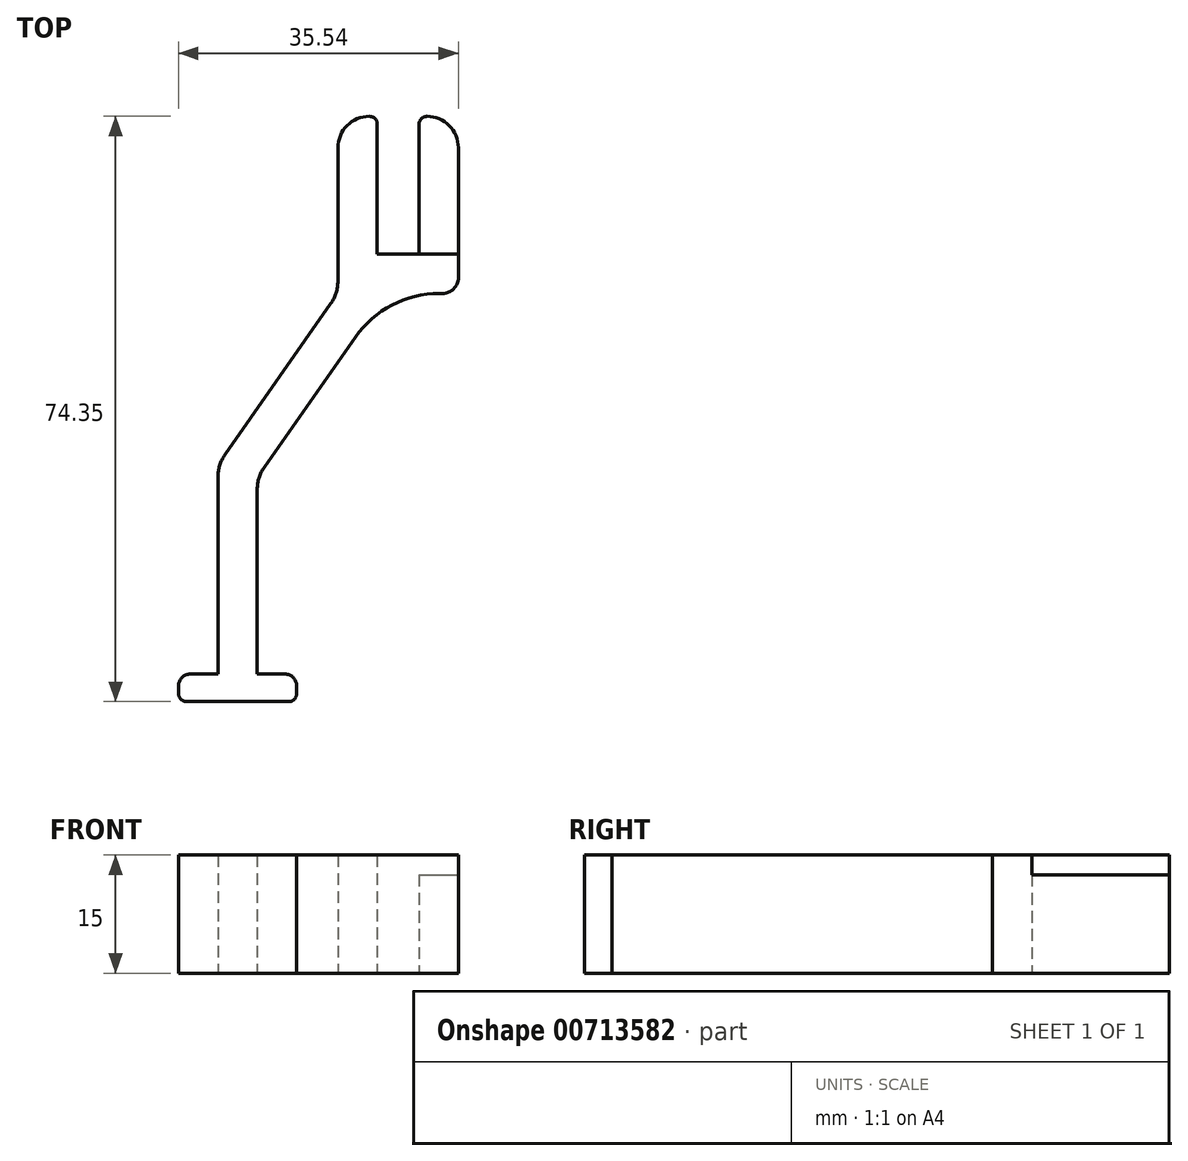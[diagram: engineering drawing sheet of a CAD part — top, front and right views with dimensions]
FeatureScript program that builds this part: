
annotation { "Feature Type Name" : "Feature", "Feature Type Description" : "" }
export const myFeature = defineFeature(function(context is Context, id is Id, definition is map)
    precondition{}
    {
        {
            var Q0;
            Q0=qCreatedBy(makeId("Top.planeOp"),FACE);
            var sketch = newSketch(context, id + "F0", { "sketchPlane" : qUnion([Q0])});
            skLineSegment(sketch, "E0", {"start": v(0, 0) * mm, "end": v(0, 16.5) * mm});
            skLineSegment(sketch, "E1", {"start": v(0, 0) * mm, "end": v(-5.3, 0) * mm});
            skLineSegment(sketch, "E2", {"start": v(-5.3, 0) * mm, "end": v(-5.3, 16.5) * mm});
            skLineSegment(sketch, "E3", {"start": v(1, 17.5) * mm, "end": v(1, 17.5) * mm});
            skLineSegment(sketch, "E4", {"start": v(5, 13.5) * mm, "end": v(5, -3.42) * mm});
            skLineSegment(sketch, "E5", {"start": v(-6.3, 17.5) * mm, "end": v(-6.3, 17.5) * mm});
            skLineSegment(sketch, "E6", {"start": v(-10.3, 13.5) * mm, "end": v(-10.3, -3) * mm});
            skLineSegment(sketch, "E7", {"start": v(5.9, -6.3) * mm, "end": v(19.34, -25.48) * mm});
            skLineSegment(sketch, "E8.0", {"start": v(2.78, -10.54) * mm, "end": v(14.34, -27.06) * mm});
            skLineSegment(sketch, "E9", {"start": v(-8.3, -5) * mm, "end": v(-7.87, -5) * mm});
            skPoint(sketch, "E10.visualSharp", {"position": v(-1.1, -5) * mm});
            skArc(sketch, "E10.filletArc", {"start": v(2.78, -10.54) * mm, "mid": v(-1.87, -6.47) * mm, "end": v(-7.87, -5) * mm});
            skPoint(sketch, "E11.visualSharp", {"position": v(-10.3, 17.5) * mm});
            skArc(sketch, "E11.filletArc", {"start": v(-6.3, 17.5) * mm, "mid": v(-9.13, 16.33) * mm, "end": v(-10.3, 13.5) * mm});
            skPoint(sketch, "E12.visualSharp", {"position": v(-5.3, 17.5) * mm});
            skArc(sketch, "E12.filletArc", {"start": v(-5.3, 16.5) * mm, "mid": v(-5.6, 17.2) * mm, "end": v(-6.3, 17.5) * mm});
            skPoint(sketch, "E13.visualSharp", {"position": v(5, 17.5) * mm});
            skArc(sketch, "E13.filletArc", {"start": v(5, 13.5) * mm, "mid": v(3.83, 16.33) * mm, "end": v(1, 17.5) * mm});
            skPoint(sketch, "E14.visualSharp", {"position": v(0, 17.5) * mm});
            skArc(sketch, "E14.filletArc", {"start": v(1, 17.5) * mm, "mid": v(0.3, 17.2) * mm, "end": v(0, 16.5) * mm});
            skPoint(sketch, "E15.visualSharp", {"position": v(5, -5) * mm});
            skArc(sketch, "E15.filletArc", {"start": v(5, -3.42) * mm, "mid": v(5.23, -4.93) * mm, "end": v(5.9, -6.3) * mm});
            skPoint(sketch, "E16.visualSharp", {"position": v(-10.3, -5) * mm});
            skArc(sketch, "E16.filletArc", {"start": v(-10.3, -3) * mm, "mid": v(-9.71, -4.41) * mm, "end": v(-8.3, -5) * mm});
            skLineSegment(sketch, "E17", {"start": v(15.24, -29.92) * mm, "end": v(15.24, -53.35) * mm});
            skLineSegment(sketch, "E18.0", {"start": v(20.24, -28.35) * mm, "end": v(20.24, -53.35) * mm});
            skPoint(sketch, "E19.visualSharp", {"position": v(20.24, -26.77) * mm});
            skArc(sketch, "E19.filletArc", {"start": v(20.24, -28.35) * mm, "mid": v(20.01, -26.84) * mm, "end": v(19.34, -25.48) * mm});
            skArc(sketch, "E20.filletArc", {"start": v(15.24, -29.92) * mm, "mid": v(15.01, -28.42) * mm, "end": v(14.34, -27.06) * mm});
            skLineSegment(sketch, "E21", {"start": v(20.24, -53.35) * mm, "end": v(23.74, -53.35) * mm});
            skLineSegment(sketch, "E22", {"start": v(15.24, -53.35) * mm, "end": v(11.74, -53.35) * mm});
            skLineSegment(sketch, "E23", {"start": v(10.24, -54.85) * mm, "end": v(10.24, -55.85) * mm});
            skLineSegment(sketch, "E24", {"start": v(25.24, -54.85) * mm, "end": v(25.24, -55.85) * mm});
            skLineSegment(sketch, "E25", {"start": v(24.24, -56.85) * mm, "end": v(11.24, -56.85) * mm});
            skPoint(sketch, "E26.visualSharp", {"position": v(10.24, -53.35) * mm});
            skArc(sketch, "E26.filletArc", {"start": v(11.74, -53.35) * mm, "mid": v(10.68, -53.79) * mm, "end": v(10.24, -54.85) * mm});
            skPoint(sketch, "E27.visualSharp", {"position": v(25.24, -53.35) * mm});
            skArc(sketch, "E27.filletArc", {"start": v(25.24, -54.85) * mm, "mid": v(24.8, -53.79) * mm, "end": v(23.74, -53.35) * mm});
            skPoint(sketch, "E28.visualSharp", {"position": v(25.24, -56.85) * mm});
            skArc(sketch, "E28.filletArc", {"start": v(24.24, -56.85) * mm, "mid": v(24.95, -56.55) * mm, "end": v(25.24, -55.85) * mm});
            skPoint(sketch, "E29.visualSharp", {"position": v(10.24, -56.85) * mm});
            skArc(sketch, "E29.filletArc", {"start": v(10.24, -55.85) * mm, "mid": v(10.54, -56.55) * mm, "end": v(11.24, -56.85) * mm});
            skSolve(sketch);
        }
        {
            var Q0;
            Q0=qSketchRegion(id+"F0",true);
            extrude(context, id + "F1", {"entities" : qUnion([Q0]), "depth" : 15 * mm, "offsetDistance" : 25 * mm});
        }
        {
            var Q0;
            Q0=makeQuery(id+"F1.opExtrude","SWEPT_BODY",BODY,{"disambiguationData":[OSD([sQuery(id+"F0.wireOp",EDGE,"E0"),sQuery(id+"F0.wireOp",EDGE,"E1"),sQuery(id+"F0.wireOp",EDGE,"E2"),sQuery(id+"F0.wireOp",EDGE,"E4"),sQuery(id+"F0.wireOp",EDGE,"E6"),sQuery(id+"F0.wireOp",EDGE,"E7"),sQuery(id+"F0.wireOp",EDGE,"E8.0"),sQuery(id+"F0.wireOp",EDGE,"E9"),sQuery(id+"F0.wireOp",EDGE,"E10.filletArc"),sQuery(id+"F0.wireOp",EDGE,"E11.filletArc"),sQuery(id+"F0.wireOp",EDGE,"E12.filletArc"),sQuery(id+"F0.wireOp",EDGE,"E13.filletArc"),sQuery(id+"F0.wireOp",EDGE,"E14.filletArc"),sQuery(id+"F0.wireOp",EDGE,"E15.filletArc"),sQuery(id+"F0.wireOp",EDGE,"E16.filletArc"),sQuery(id+"F0.wireOp",EDGE,"E17"),sQuery(id+"F0.wireOp",EDGE,"E18.0"),sQuery(id+"F0.wireOp",EDGE,"E19.filletArc"),sQuery(id+"F0.wireOp",EDGE,"E20.filletArc"),sQuery(id+"F0.wireOp",EDGE,"E21"),sQuery(id+"F0.wireOp",EDGE,"E22"),sQuery(id+"F0.wireOp",EDGE,"E23"),sQuery(id+"F0.wireOp",EDGE,"E24"),sQuery(id+"F0.wireOp",EDGE,"E25"),sQuery(id+"F0.wireOp",EDGE,"E26.filletArc"),sQuery(id+"F0.wireOp",EDGE,"E27.filletArc"),sQuery(id+"F0.wireOp",EDGE,"E28.filletArc"),sQuery(id+"F0.wireOp",EDGE,"E29.filletArc")])]});
            var Q1;
            Q1=makeQuery(id+"F1.opExtrude","SWEPT_FACE",FACE,{"disambiguationData":[OSD([sQuery(id+"F0.wireOp",EDGE,"E6")])]});
            mirror(context, id + "F2", {"entities" : qUnion([Q0]), "mirrorPlane" : qUnion([Q1])});
        }
        {
            var Q0;
            Q0=makeQuery(id+"F1.opExtrude","SWEPT_BODY",BODY,{"disambiguationData":[OSD([sQuery(id+"F0.wireOp",EDGE,"E0"),sQuery(id+"F0.wireOp",EDGE,"E1"),sQuery(id+"F0.wireOp",EDGE,"E2"),sQuery(id+"F0.wireOp",EDGE,"E4"),sQuery(id+"F0.wireOp",EDGE,"E6"),sQuery(id+"F0.wireOp",EDGE,"E7"),sQuery(id+"F0.wireOp",EDGE,"E8.0"),sQuery(id+"F0.wireOp",EDGE,"E9"),sQuery(id+"F0.wireOp",EDGE,"E10.filletArc"),sQuery(id+"F0.wireOp",EDGE,"E11.filletArc"),sQuery(id+"F0.wireOp",EDGE,"E12.filletArc"),sQuery(id+"F0.wireOp",EDGE,"E13.filletArc"),sQuery(id+"F0.wireOp",EDGE,"E14.filletArc"),sQuery(id+"F0.wireOp",EDGE,"E15.filletArc"),sQuery(id+"F0.wireOp",EDGE,"E16.filletArc"),sQuery(id+"F0.wireOp",EDGE,"E17"),sQuery(id+"F0.wireOp",EDGE,"E18.0"),sQuery(id+"F0.wireOp",EDGE,"E19.filletArc"),sQuery(id+"F0.wireOp",EDGE,"E20.filletArc"),sQuery(id+"F0.wireOp",EDGE,"E21"),sQuery(id+"F0.wireOp",EDGE,"E22"),sQuery(id+"F0.wireOp",EDGE,"E23"),sQuery(id+"F0.wireOp",EDGE,"E24"),sQuery(id+"F0.wireOp",EDGE,"E25"),sQuery(id+"F0.wireOp",EDGE,"E26.filletArc"),sQuery(id+"F0.wireOp",EDGE,"E27.filletArc"),sQuery(id+"F0.wireOp",EDGE,"E28.filletArc"),sQuery(id+"F0.wireOp",EDGE,"E29.filletArc")])]});
            deleteBodies(context, id + "F3", {"entities" : qUnion([Q0])});
        }
        {
            var Q0;
            Q0=makeQuery(id+"F2.opPattern","COPY",FACE,{"derivedFrom":makeQuery(id+"F1.opExtrude","SWEPT_FACE",FACE,{"disambiguationData":[OSD([sQuery(id+"F0.wireOp",EDGE,"E6")])]}),"instanceName":"1"});
            var sketch = newSketch(context, id + "F4", { "sketchPlane" : qUnion([Q0])});
            skPoint(sketch, "E30.0", {"position": v(17.5, 15) * mm});
            skPoint(sketch, "E31.0", {"position": v(0, 15) * mm});
            skLineSegment(sketch, "E32", {"start": v(17.5, 15) * mm, "end": v(0, 15) * mm});
            skLineSegment(sketch, "E33", {"start": v(0, 15) * mm, "end": v(0, 12.5) * mm});
            skLineSegment(sketch, "E34", {"start": v(0, 12.5) * mm, "end": v(17.5, 12.5) * mm});
            skLineSegment(sketch, "E35", {"start": v(17.5, 12.5) * mm, "end": v(17.5, 15) * mm});
            skSolve(sketch);
        }
        {
            var Q0;
            Q0=qSketchRegion(id+"F4",true);
            extrude(context, id + "F5", {"entities" : qUnion([Q0]), "operationType" : NewBodyOperationType.REMOVE, "oppositeDirection" : true, "depth" : 5.7 * mm, "offsetDistance" : 25 * mm});
        }
    });
